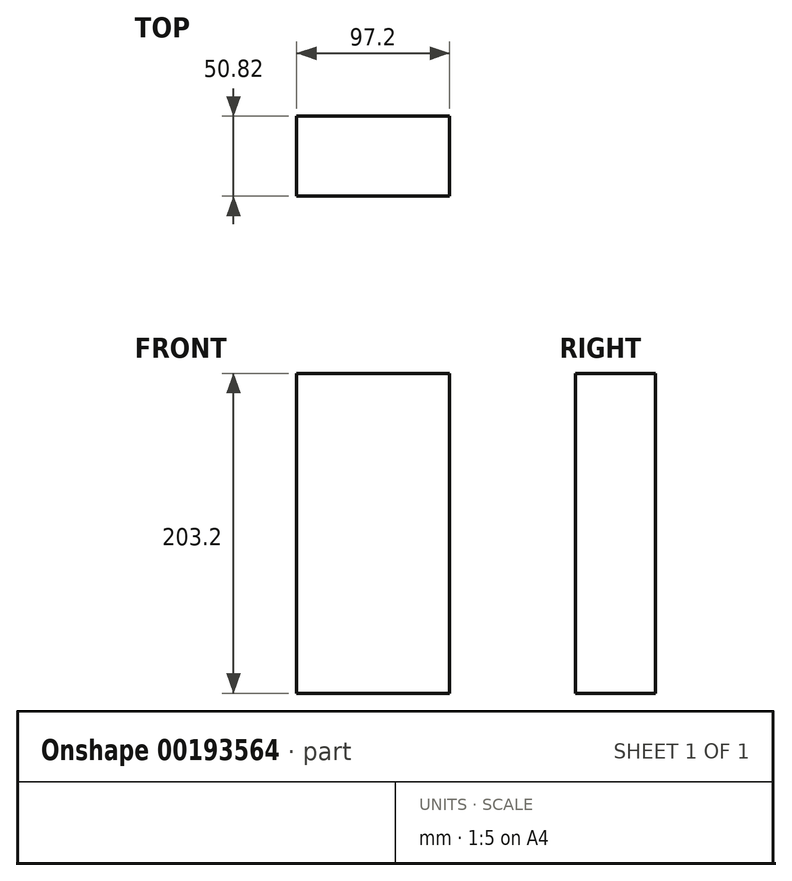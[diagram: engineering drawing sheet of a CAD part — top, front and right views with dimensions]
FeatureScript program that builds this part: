
annotation { "Feature Type Name" : "Feature", "Feature Type Description" : "" }
export const myFeature = defineFeature(function(context is Context, id is Id, definition is map)
    precondition{}
    {
        {
            var Q0;
            Q0=qCreatedBy(makeId("Top.planeOp"),FACE);
            var sketch = newSketch(context, id + "F0", { "sketchPlane" : qUnion([Q0])});
            skLineSegment(sketch, "E0.bottom", {"start": v(48.6, 25.4) * mm, "end": v(-48.6, 25.4) * mm});
            skLineSegment(sketch, "E0.top", {"start": v(48.6, -25.4) * mm, "end": v(-48.6, -25.4) * mm});
            skLineSegment(sketch, "E0.left", {"start": v(48.6, 25.4) * mm, "end": v(48.6, -25.4) * mm});
            skLineSegment(sketch, "E0.right", {"start": v(-48.6, 25.4) * mm, "end": v(-48.6, -25.4) * mm});
            skPoint(sketch, "E0.middle", {"position": v(0, 0) * mm});
            skSolve(sketch);
        }
        {
            var Q0;
            Q0 = qSketchRegion(id + "F0", true);
            extrude(context, id + "F1", {"entities" : qUnion([Q0]), "depth" : 203.2 * mm});
        }
    });
